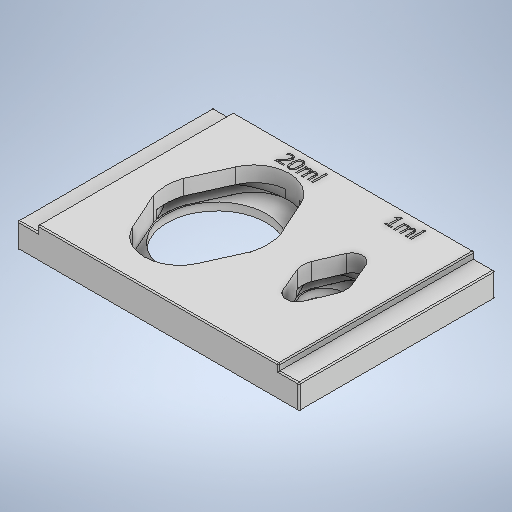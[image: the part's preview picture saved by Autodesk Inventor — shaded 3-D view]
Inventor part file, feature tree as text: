
AUTODESK INVENTOR PART (.ipt)
format: ipt  version: 2025 (Build 290162000, 162)  size: 645,120 bytes
history: native  units: mm
features: extrude x10, sketch x10, fillet x4, projected_geometry x1
ambient origin geometry x8: Origin, YZ Plane, XZ Plane, XY Plane, X Axis, Y Axis, Z Axis, Center Point
bodies: Volumenkörper1 (feature_tree)
feature tree (25):
  extrude  "Extrusion1"  Depth=50.0mm
  extrude  "Extrusion2"  Depth=25.4mm
  extrude  "Extrusion3"  Depth=10.0mm
  extrude  "Extrusion4"  Depth=2.0mm TaperAngle=0.0deg
  extrude  "Extrusion5"  Depth=1.57mm TaperAngle=0.0deg
  extrude  "Extrusion6"  Depth=0.53mm TaperAngle=0.0deg
  fillet  "Rundung1"  Radius=0.3mm
  fillet  "Rundung2"  Radius=0.3mm
  extrude  "Extrusion10"  TaperAngle=0.0deg  [1 undecoded]
  extrude  "Extrusion11"  Depth=5.2mm
  extrude  "Extrusion12"  Depth=1.65mm TaperAngle=0.0deg
  fillet  "Rundung3"  Radius=0.3mm
  fillet  "Rundung4"  Radius=0.3mm
  extrude  "Extrusion13"  Depth=1.5mm
  sketch  "Skizze1"  dims[d0=72.0mm d1=50.0mm]
  sketch  "Skizze2"  dims[d2=2.0mm d3=0.0mm d4=25.4mm]
  sketch  "Skizze3"  dims[d5=10.4mm d6=10.0mm]
  sketch  "Skizze4"  dims[d7=17.5mm d8=2.0mm d9=0.0mm]
  sketch  "Skizze5"  dims[d10=1.57mm d11=0.0mm d20=1.57mm d21=0.0mm]
  sketch  "Skizze6"  dims[d41=1.57mm d42=0.0mm d43=0.53mm d44=0.0mm d59=0.3mm d60=0.3mm]
  sketch  "Skizze10"  dims[d96=2.25mm d97=0.0mm d98=0.0mm]
  sketch  "Skizze11"  dims[d102=4.37mm d103=0.0mm d104=5.2mm]
  sketch  "Skizze12"  dims[d105=5.2mm d106=1.65mm d107=0.0mm d108=0.3mm d109=0.3mm]
  projected_geometry  "Projizierte Kontur7"
  sketch  "Skizze13"  dims[d110=1.5mm d111=1.5mm d112=0.5mm d113=0.0mm d45=0.5mm d46=0.872665mm]
note: 1 required parameter value undecoded (feature->parameter linkage not recoverable at this tier; creation-order binding heuristic only, values carry confidence <= 0.55)
